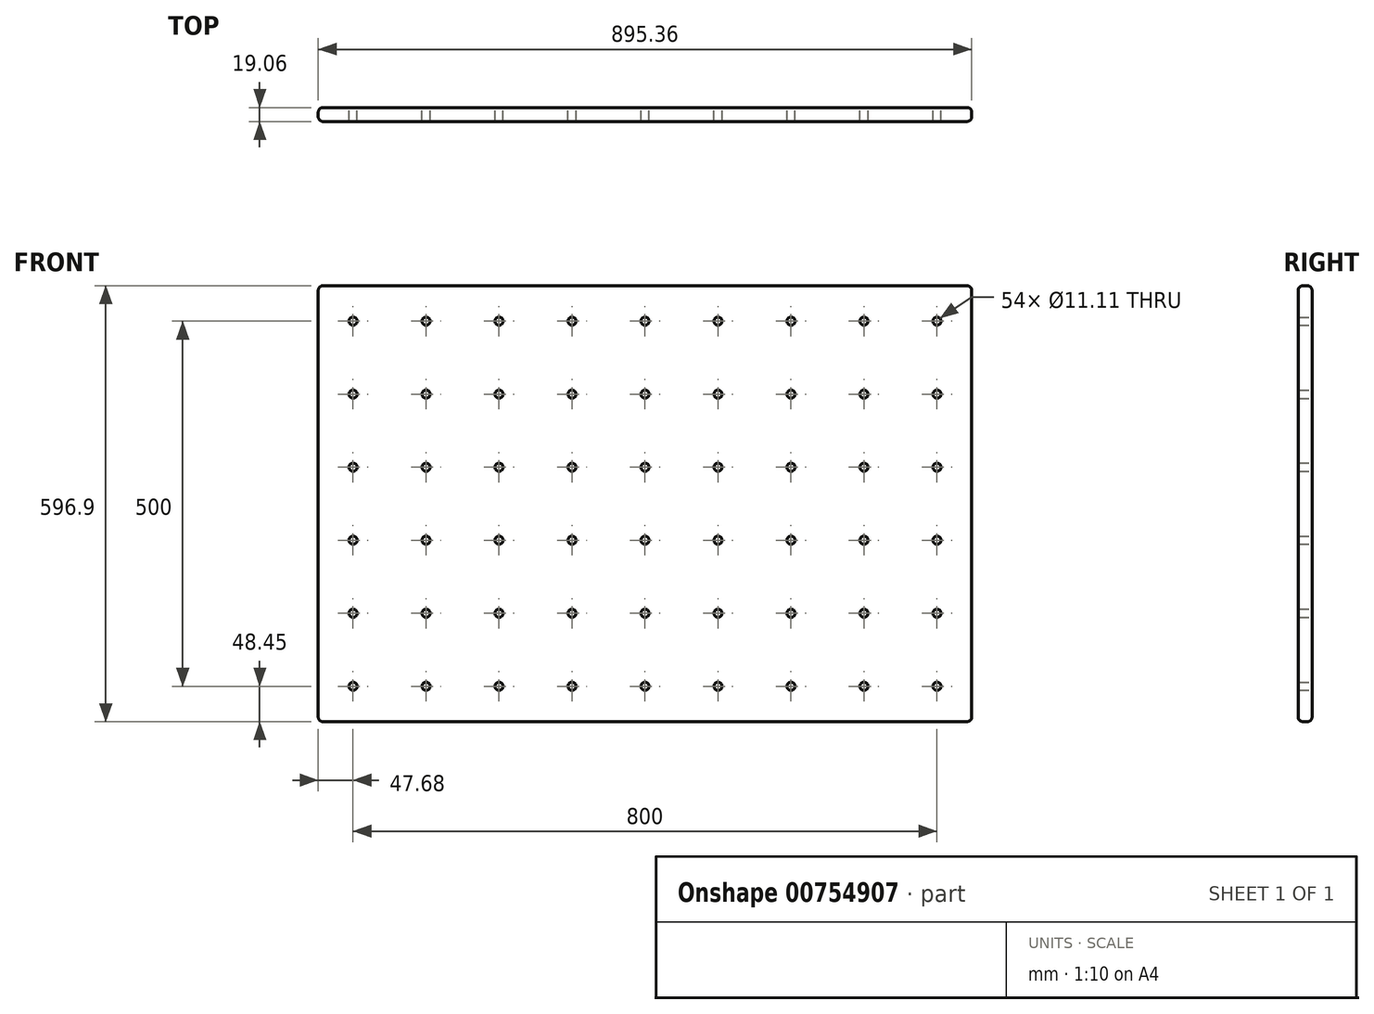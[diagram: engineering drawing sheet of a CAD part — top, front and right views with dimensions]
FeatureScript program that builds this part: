
annotation { "Feature Type Name" : "Feature", "Feature Type Description" : "" }
export const myFeature = defineFeature(function(context is Context, id is Id, definition is map)
    precondition{}
    {
        {
            var Q0;
            Q0=qCreatedBy(makeId("Front.planeOp"),FACE);
            var sketch = newSketch(context, id + "F0", { "sketchPlane" : qUnion([Q0])});
            skLineSegment(sketch, "E0.bottom", {"start": v(-447.68, 298.45) * mm, "end": v(447.68, 298.45) * mm});
            skLineSegment(sketch, "E0.top", {"start": v(-447.68, -298.45) * mm, "end": v(447.67, -298.45) * mm});
            skLineSegment(sketch, "E0.left", {"start": v(-447.68, 298.45) * mm, "end": v(-447.68, -298.45) * mm});
            skLineSegment(sketch, "E0.right", {"start": v(447.68, 298.45) * mm, "end": v(447.67, -298.45) * mm});
            skCircle(sketch, "E1", {"center": v(400, -250) * mm, "radius": 5.56 * mm});
            skCircle(sketch, "E2.0.1.0", {"center": v(400, -150) * mm, "radius": 5.56 * mm});
            skCircle(sketch, "E2.0.2.0", {"center": v(400, -50) * mm, "radius": 5.56 * mm});
            skCircle(sketch, "E2.0.3.0", {"center": v(400, 50) * mm, "radius": 5.56 * mm});
            skCircle(sketch, "E2.0.4.0", {"center": v(400, 150) * mm, "radius": 5.56 * mm});
            skCircle(sketch, "E2.0.5.0", {"center": v(400, 250) * mm, "radius": 5.56 * mm});
            skCircle(sketch, "E2.1.0.0", {"center": v(300, -250) * mm, "radius": 5.56 * mm});
            skCircle(sketch, "E2.1.1.0", {"center": v(300, -150) * mm, "radius": 5.56 * mm});
            skCircle(sketch, "E2.1.2.0", {"center": v(300, -50) * mm, "radius": 5.56 * mm});
            skCircle(sketch, "E2.1.3.0", {"center": v(300, 50) * mm, "radius": 5.56 * mm});
            skCircle(sketch, "E2.1.4.0", {"center": v(300, 150) * mm, "radius": 5.56 * mm});
            skCircle(sketch, "E2.1.5.0", {"center": v(300, 250) * mm, "radius": 5.56 * mm});
            skCircle(sketch, "E2.2.0.0", {"center": v(200, -250) * mm, "radius": 5.56 * mm});
            skCircle(sketch, "E2.2.1.0", {"center": v(200, -150) * mm, "radius": 5.56 * mm});
            skCircle(sketch, "E2.2.2.0", {"center": v(200, -50) * mm, "radius": 5.56 * mm});
            skCircle(sketch, "E2.2.3.0", {"center": v(200, 50) * mm, "radius": 5.56 * mm});
            skCircle(sketch, "E2.2.4.0", {"center": v(200, 150) * mm, "radius": 5.56 * mm});
            skCircle(sketch, "E2.2.5.0", {"center": v(200, 250) * mm, "radius": 5.56 * mm});
            skCircle(sketch, "E2.3.0.0", {"center": v(100, -250) * mm, "radius": 5.56 * mm});
            skCircle(sketch, "E2.3.1.0", {"center": v(100, -150) * mm, "radius": 5.56 * mm});
            skCircle(sketch, "E2.3.2.0", {"center": v(100, -50) * mm, "radius": 5.56 * mm});
            skCircle(sketch, "E2.3.3.0", {"center": v(100, 50) * mm, "radius": 5.56 * mm});
            skCircle(sketch, "E2.3.4.0", {"center": v(100, 150) * mm, "radius": 5.56 * mm});
            skCircle(sketch, "E2.3.5.0", {"center": v(100, 250) * mm, "radius": 5.56 * mm});
            skCircle(sketch, "E2.4.0.0", {"center": v(0, -250) * mm, "radius": 5.56 * mm});
            skCircle(sketch, "E2.4.1.0", {"center": v(0, -150) * mm, "radius": 5.56 * mm});
            skCircle(sketch, "E2.4.2.0", {"center": v(0, -50) * mm, "radius": 5.56 * mm});
            skCircle(sketch, "E2.4.3.0", {"center": v(0, 50) * mm, "radius": 5.56 * mm});
            skCircle(sketch, "E2.4.4.0", {"center": v(0, 150) * mm, "radius": 5.56 * mm});
            skCircle(sketch, "E2.4.5.0", {"center": v(0, 250) * mm, "radius": 5.56 * mm});
            skCircle(sketch, "E2.5.0.0", {"center": v(-100, -250) * mm, "radius": 5.56 * mm});
            skCircle(sketch, "E2.5.1.0", {"center": v(-100, -150) * mm, "radius": 5.56 * mm});
            skCircle(sketch, "E2.5.2.0", {"center": v(-100, -50) * mm, "radius": 5.56 * mm});
            skCircle(sketch, "E2.5.3.0", {"center": v(-100, 50) * mm, "radius": 5.56 * mm});
            skCircle(sketch, "E2.5.4.0", {"center": v(-100, 150) * mm, "radius": 5.56 * mm});
            skCircle(sketch, "E2.5.5.0", {"center": v(-100, 250) * mm, "radius": 5.56 * mm});
            skCircle(sketch, "E2.6.0.0", {"center": v(-200, -250) * mm, "radius": 5.56 * mm});
            skCircle(sketch, "E2.6.1.0", {"center": v(-200, -150) * mm, "radius": 5.56 * mm});
            skCircle(sketch, "E2.6.2.0", {"center": v(-200, -50) * mm, "radius": 5.56 * mm});
            skCircle(sketch, "E2.6.3.0", {"center": v(-200, 50) * mm, "radius": 5.56 * mm});
            skCircle(sketch, "E2.6.4.0", {"center": v(-200, 150) * mm, "radius": 5.56 * mm});
            skCircle(sketch, "E2.6.5.0", {"center": v(-200, 250) * mm, "radius": 5.56 * mm});
            skCircle(sketch, "E2.7.0.0", {"center": v(-300, -250) * mm, "radius": 5.56 * mm});
            skCircle(sketch, "E2.7.1.0", {"center": v(-300, -150) * mm, "radius": 5.56 * mm});
            skCircle(sketch, "E2.7.2.0", {"center": v(-300, -50) * mm, "radius": 5.56 * mm});
            skCircle(sketch, "E2.7.3.0", {"center": v(-300, 50) * mm, "radius": 5.56 * mm});
            skCircle(sketch, "E2.7.4.0", {"center": v(-300, 150) * mm, "radius": 5.56 * mm});
            skCircle(sketch, "E2.7.5.0", {"center": v(-300, 250) * mm, "radius": 5.56 * mm});
            skCircle(sketch, "E2.8.0.0", {"center": v(-400, -250) * mm, "radius": 5.56 * mm});
            skCircle(sketch, "E2.8.1.0", {"center": v(-400, -150) * mm, "radius": 5.56 * mm});
            skCircle(sketch, "E2.8.2.0", {"center": v(-400, -50) * mm, "radius": 5.56 * mm});
            skCircle(sketch, "E2.8.3.0", {"center": v(-400, 50) * mm, "radius": 5.56 * mm});
            skCircle(sketch, "E2.8.4.0", {"center": v(-400, 150) * mm, "radius": 5.56 * mm});
            skCircle(sketch, "E2.8.5.0", {"center": v(-400, 250) * mm, "radius": 5.56 * mm});
            skLineSegment(sketch, "E2.direction1", {"start": v(400, -250) * mm, "end": v(300, -250) * mm, "construction": true});
            skLineSegment(sketch, "E2.direction2", {"start": v(400, -250) * mm, "end": v(400, -150) * mm, "construction": true});
            skSolve(sketch);
        }
        {
            var Q0;
            Q0=makeQuery(id+"F0.imprint","IMPRINT",FACE,{"disambiguationData":[TD([[makeQuery(id+"F0.imprint","IMPRINT",EDGE,{"derivedFrom":sQuery(id+"F0.wireOp",EDGE,"E0.bottom")}),-1.0]])]});
            extrude(context, id + "F1", {"entities" : qUnion([Q0]), "endBound" : BoundingType.SYMMETRIC, "depth" : 19.05 * mm});
        }
        {
            var Q0;
            Q0=makeQuery(id+"F1.opExtrude","SWEPT_EDGE",EDGE,{"disambiguationData":[OSD([sQuery(id+"F0.wireOp",EDGE,"E0.bottom"),sQuery(id+"F0.wireOp",EDGE,"E0.left")])]});
            var Q1;
            Q1=makeQuery(id+"F1.opExtrude","CAP_EDGE",EDGE,{"disambiguationData":[OSD([sQuery(id+"F0.wireOp",EDGE,"E0.bottom")])],"isStart":true});
            var Q2;
            Q2=makeQuery(id+"F1.opExtrude","CAP_EDGE",EDGE,{"disambiguationData":[OSD([sQuery(id+"F0.wireOp",EDGE,"E0.left")])],"isStart":true});
            var Q3;
            Q3=makeQuery(id+"F1.opExtrude","CAP_EDGE",EDGE,{"disambiguationData":[OSD([sQuery(id+"F0.wireOp",EDGE,"E0.left")])],"isStart":false});
            var Q4;
            Q4=makeQuery(id+"F1.opExtrude","SWEPT_EDGE",EDGE,{"disambiguationData":[OSD([sQuery(id+"F0.wireOp",EDGE,"E0.bottom"),sQuery(id+"F0.wireOp",EDGE,"E0.right")])]});
            var Q5;
            Q5=makeQuery(id+"F1.opExtrude","CAP_EDGE",EDGE,{"disambiguationData":[OSD([sQuery(id+"F0.wireOp",EDGE,"E0.bottom")])],"isStart":false});
            var Q6;
            Q6=makeQuery(id+"F1.opExtrude","CAP_EDGE",EDGE,{"disambiguationData":[OSD([sQuery(id+"F0.wireOp",EDGE,"E0.right")])],"isStart":false});
            var Q7;
            Q7=makeQuery(id+"F1.opExtrude","CAP_EDGE",EDGE,{"disambiguationData":[OSD([sQuery(id+"F0.wireOp",EDGE,"E0.top")])],"isStart":false});
            var Q8;
            Q8=makeQuery(id+"F1.opExtrude","SWEPT_EDGE",EDGE,{"disambiguationData":[OSD([sQuery(id+"F0.wireOp",EDGE,"E0.top"),sQuery(id+"F0.wireOp",EDGE,"E0.left")])]});
            var Q9;
            Q9=makeQuery(id+"F1.opExtrude","CAP_EDGE",EDGE,{"disambiguationData":[OSD([sQuery(id+"F0.wireOp",EDGE,"E0.top")])],"isStart":true});
            var Q10;
            Q10=makeQuery(id+"F1.opExtrude","SWEPT_EDGE",EDGE,{"disambiguationData":[OSD([sQuery(id+"F0.wireOp",EDGE,"E0.top"),sQuery(id+"F0.wireOp",EDGE,"E0.right")])]});
            var Q11;
            Q11=makeQuery(id+"F1.opExtrude","CAP_EDGE",EDGE,{"disambiguationData":[OSD([sQuery(id+"F0.wireOp",EDGE,"E0.right")])],"isStart":true});
            fillet(context, id + "F2", {"entities" : qUnion([Q0, Q1, Q2, Q3, Q4, Q5, Q6, Q7, Q8, Q9, Q10, Q11]), "radius" : 6.35 * mm, "tangentPropagation" : true, "allowEdgeOverflow" : false});
        }
        {
            var Q0;
            Q0=makeQuery(id+"F1.opExtrude","CAP_FACE",FACE,{"disambiguationData":[OSD([sQuery(id+"F0.wireOp",EDGE,"E0.bottom"),sQuery(id+"F0.wireOp",EDGE,"E0.top"),sQuery(id+"F0.wireOp",EDGE,"E0.left"),sQuery(id+"F0.wireOp",EDGE,"E0.right"),sQuery(id+"F0.wireOp",EDGE,"E1"),sQuery(id+"F0.wireOp",EDGE,"E2.0.1.0"),sQuery(id+"F0.wireOp",EDGE,"E2.0.2.0"),sQuery(id+"F0.wireOp",EDGE,"E2.0.3.0"),sQuery(id+"F0.wireOp",EDGE,"E2.0.4.0"),sQuery(id+"F0.wireOp",EDGE,"E2.0.5.0"),sQuery(id+"F0.wireOp",EDGE,"E2.1.0.0"),sQuery(id+"F0.wireOp",EDGE,"E2.1.1.0"),sQuery(id+"F0.wireOp",EDGE,"E2.1.2.0"),sQuery(id+"F0.wireOp",EDGE,"E2.1.3.0"),sQuery(id+"F0.wireOp",EDGE,"E2.1.4.0"),sQuery(id+"F0.wireOp",EDGE,"E2.1.5.0"),sQuery(id+"F0.wireOp",EDGE,"E2.2.0.0"),sQuery(id+"F0.wireOp",EDGE,"E2.2.1.0"),sQuery(id+"F0.wireOp",EDGE,"E2.2.2.0"),sQuery(id+"F0.wireOp",EDGE,"E2.2.3.0"),sQuery(id+"F0.wireOp",EDGE,"E2.2.4.0"),sQuery(id+"F0.wireOp",EDGE,"E2.2.5.0"),sQuery(id+"F0.wireOp",EDGE,"E2.3.0.0"),sQuery(id+"F0.wireOp",EDGE,"E2.3.1.0"),sQuery(id+"F0.wireOp",EDGE,"E2.3.2.0"),sQuery(id+"F0.wireOp",EDGE,"E2.3.3.0"),sQuery(id+"F0.wireOp",EDGE,"E2.3.4.0"),sQuery(id+"F0.wireOp",EDGE,"E2.3.5.0"),sQuery(id+"F0.wireOp",EDGE,"E2.4.0.0"),sQuery(id+"F0.wireOp",EDGE,"E2.4.1.0"),sQuery(id+"F0.wireOp",EDGE,"E2.4.2.0"),sQuery(id+"F0.wireOp",EDGE,"E2.4.3.0"),sQuery(id+"F0.wireOp",EDGE,"E2.4.4.0"),sQuery(id+"F0.wireOp",EDGE,"E2.4.5.0"),sQuery(id+"F0.wireOp",EDGE,"E2.5.0.0"),sQuery(id+"F0.wireOp",EDGE,"E2.5.1.0"),sQuery(id+"F0.wireOp",EDGE,"E2.5.2.0"),sQuery(id+"F0.wireOp",EDGE,"E2.5.3.0"),sQuery(id+"F0.wireOp",EDGE,"E2.5.4.0"),sQuery(id+"F0.wireOp",EDGE,"E2.5.5.0"),sQuery(id+"F0.wireOp",EDGE,"E2.6.0.0"),sQuery(id+"F0.wireOp",EDGE,"E2.6.1.0"),sQuery(id+"F0.wireOp",EDGE,"E2.6.2.0"),sQuery(id+"F0.wireOp",EDGE,"E2.6.3.0"),sQuery(id+"F0.wireOp",EDGE,"E2.6.4.0"),sQuery(id+"F0.wireOp",EDGE,"E2.6.5.0"),sQuery(id+"F0.wireOp",EDGE,"E2.7.0.0"),sQuery(id+"F0.wireOp",EDGE,"E2.7.1.0"),sQuery(id+"F0.wireOp",EDGE,"E2.7.2.0"),sQuery(id+"F0.wireOp",EDGE,"E2.7.3.0"),sQuery(id+"F0.wireOp",EDGE,"E2.7.4.0"),sQuery(id+"F0.wireOp",EDGE,"E2.7.5.0"),sQuery(id+"F0.wireOp",EDGE,"E2.8.0.0"),sQuery(id+"F0.wireOp",EDGE,"E2.8.1.0"),sQuery(id+"F0.wireOp",EDGE,"E2.8.2.0"),sQuery(id+"F0.wireOp",EDGE,"E2.8.3.0"),sQuery(id+"F0.wireOp",EDGE,"E2.8.4.0"),sQuery(id+"F0.wireOp",EDGE,"E2.8.5.0")])],"isStart":false});
            var sketch = newSketch(context, id + "F3", { "sketchPlane" : qUnion([Q0])});
            skLineSegment(sketch, "E3", {"start": v(-400.05, 200) * mm, "end": v(0, 200) * mm});
            skLineSegment(sketch, "E4.MirrorCS", {"start": v(400.05, 200) * mm, "end": v(0, 200) * mm});
            skLineSegment(sketch, "E5", {"start": v(-400.05, 200) * mm, "end": v(-400.05, 213.59) * mm});
            skLineSegment(sketch, "E6", {"start": v(-400.05, 200) * mm, "end": v(-404.39, 200) * mm});
            skSolve(sketch);
        }
    });
